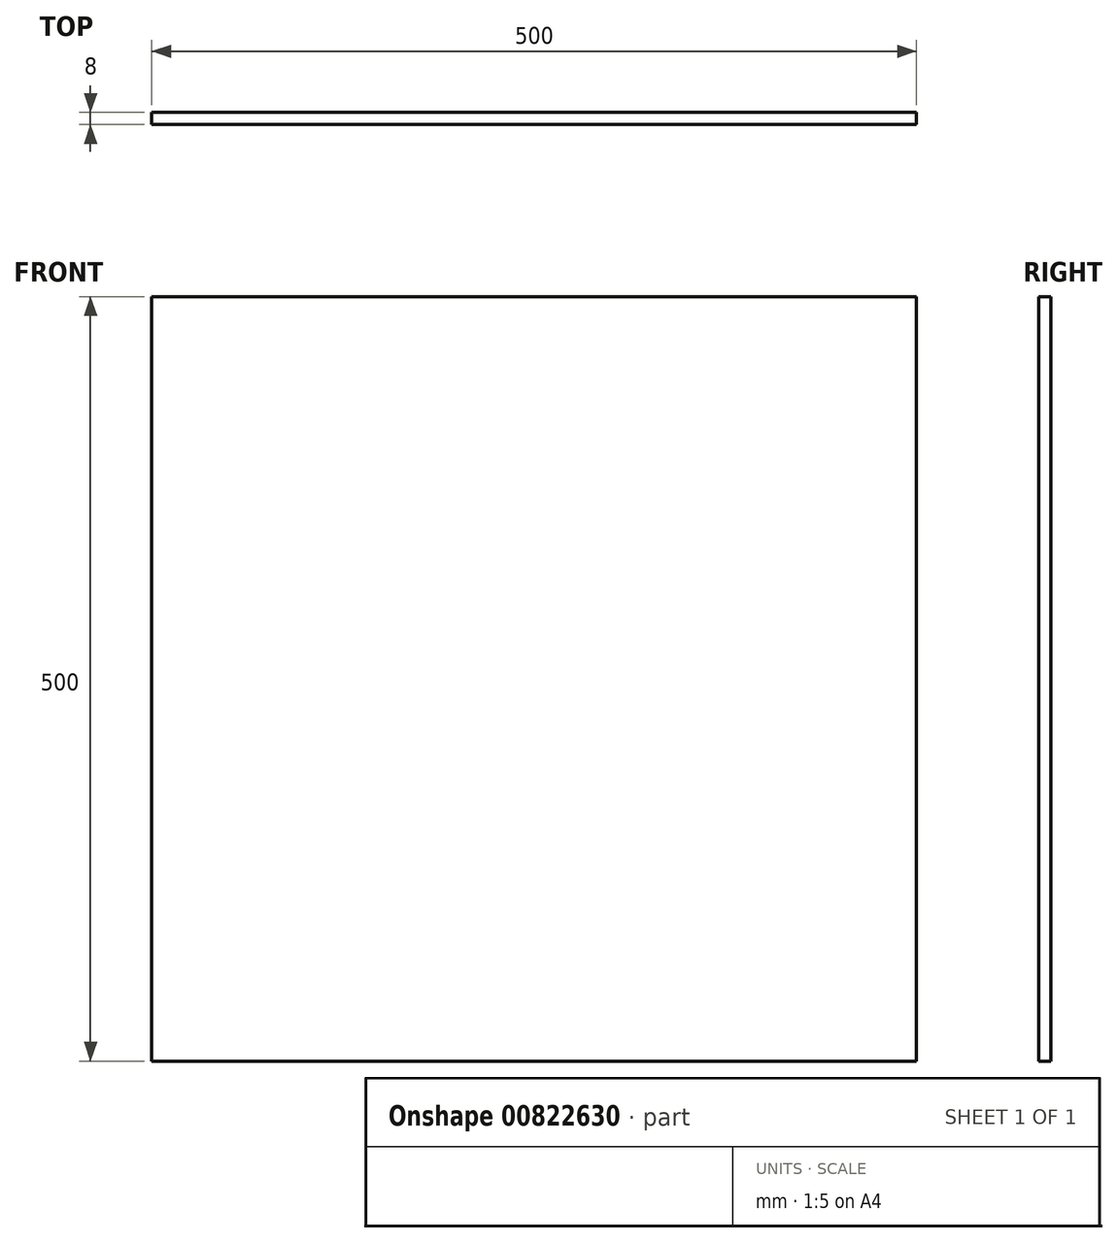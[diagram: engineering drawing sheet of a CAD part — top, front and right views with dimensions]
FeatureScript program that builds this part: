
annotation { "Feature Type Name" : "Feature", "Feature Type Description" : "" }
export const myFeature = defineFeature(function(context is Context, id is Id, definition is map)
    precondition{}
    {
        {
            var Q0;
            Q0=qCreatedBy(makeId("Front.planeOp"),FACE);
            var sketch = newSketch(context, id + "F0", { "sketchPlane" : qUnion([Q0])});
            skLineSegment(sketch, "E0.bottom", {"start": v(-250, 250) * mm, "end": v(250, 250) * mm});
            skLineSegment(sketch, "E0.top", {"start": v(-250, -250) * mm, "end": v(250, -250) * mm});
            skLineSegment(sketch, "E0.left", {"start": v(-250, 250) * mm, "end": v(-250, -250) * mm});
            skLineSegment(sketch, "E0.right", {"start": v(250, 250) * mm, "end": v(250, -250) * mm});
            skPoint(sketch, "E0.middle", {"position": v(0, 0) * mm});
            skSolve(sketch);
        }
        {
            var Q0;
            Q0=makeQuery(id+"F0.imprint","IMPRINT",FACE,{"disambiguationData":[TD([[makeQuery(id+"F0.imprint","IMPRINT",EDGE,{"derivedFrom":sQuery(id+"F0.wireOp",EDGE,"E0.bottom")}),-1.0]])]});
            extrude(context, id + "F1", {"entities" : qUnion([Q0]), "depth" : 8 * mm, "offsetDistance" : 25 * mm, "symmetric" : true});
        }
    });
